# Revit family: Shower_Wall_Caroma Pin Adjustable
name_source: partatom
category: Plumbing Fixtures
revit_build: Autodesk Revit MEP 2014 (Build: 20140709_2115(x64)
units: mm (PartAtom-declared; Revit-internal decimal feet)

## types (3) — shared parameters
Assembly Code = D2010710
CW Connection = Yes
ConnectorDiameter = 20 mm  [stored 0.0656168 ft]
Default Elevation = 1800 mm  [stored 5.90551 ft]
Description = TBC
HW Connection = Yes
Manufacturer = Caroma
Material_ANZRS = Metal-Chrome-Caroma
ModifiedIssue_ANZRS = 20160203.54 $
Type Comments = Caroma Pin Adjustable Wall Shower
URL = http://specify.caroma.com.au
Vent Connection = No
WELSRating_ANZRS = WELS 3 star rated, 9L/min
Waste Connection = No
zero-valued in all types: CWFU, Cost, HWFU

## per-type parameters (varying)
| type | Model |
| Chrome | 87259C3A |
| Black | 87259B3A |
| White | 87259W3A |

note: [stored X ft] marks values corroborated as IEEE doubles in the binary element streams (Revit-internal decimal feet)

## geometry (parser evidence)
native form markers: Blend x10, Sweep x1
no freeform markers — native parametric forms only
